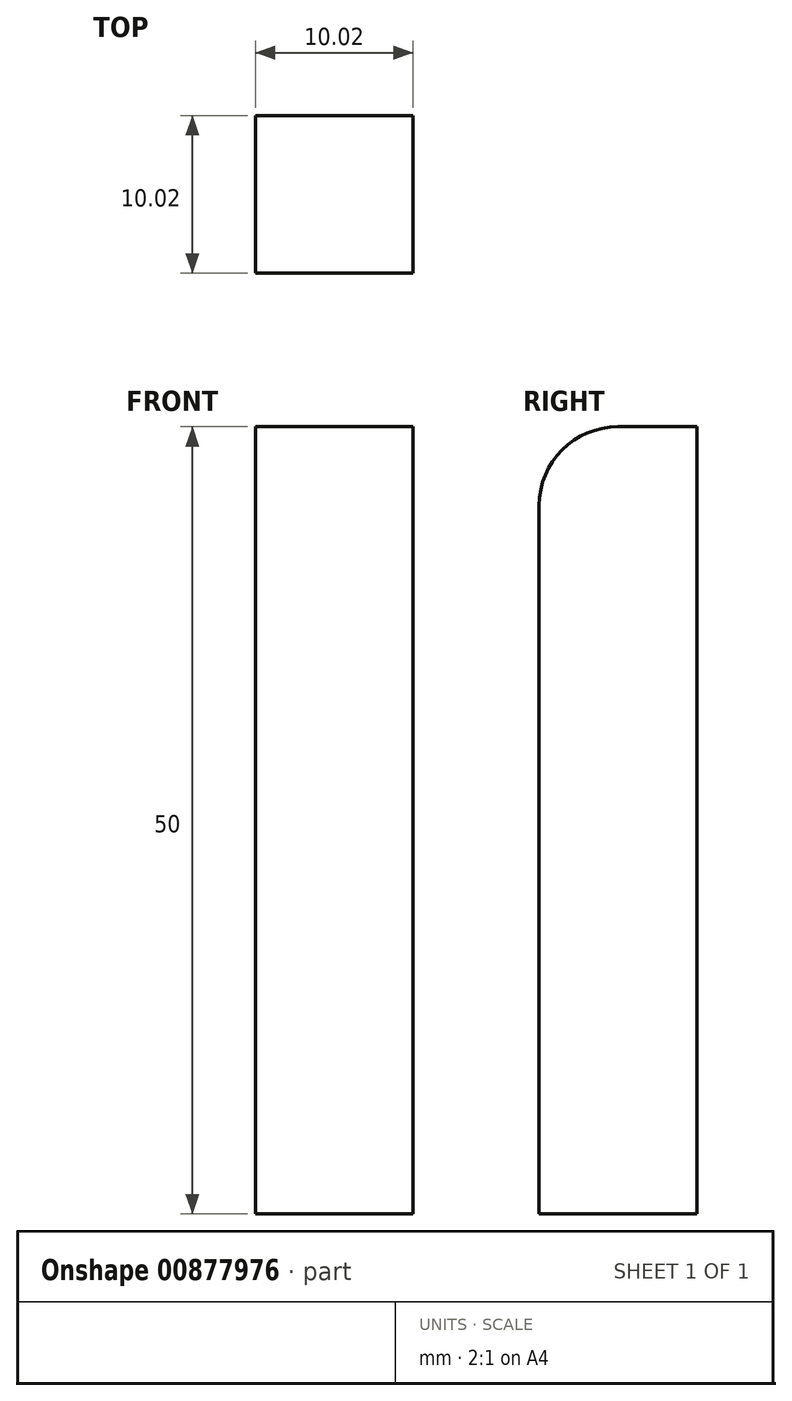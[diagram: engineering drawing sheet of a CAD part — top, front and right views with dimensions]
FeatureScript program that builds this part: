
annotation { "Feature Type Name" : "Feature", "Feature Type Description" : "" }
export const myFeature = defineFeature(function(context is Context, id is Id, definition is map)
    precondition{}
    {
        {
            var Q0;
            Q0=qCreatedBy(makeId("Top.planeOp"),FACE);
            var sketch = newSketch(context, id + "F0", { "sketchPlane" : qUnion([Q0])});
            skCircle(sketch, "E0", {"center": v(0, 0) * mm, "radius": 15 * mm});
            skSolve(sketch);
        }
        {
            var Q0;
            Q0=qSketchRegion(id+"F0",true);
            extrude(context, id + "F1", {"entities" : qUnion([Q0]), "endBound" : BoundingType.SYMMETRIC, "depth" : 25 * mm, "offsetDistance" : 25 * mm});
        }
        {
            var Q0;
            Q0=makeQuery(id+"F1.opExtrude","CAP_FACE",FACE,{"disambiguationData":[OSD([sQuery(id+"F0.wireOp",EDGE,"E0")])],"isStart":false});
            var sketch = newSketch(context, id + "F2", { "sketchPlane" : qUnion([Q0])});
            skLineSegment(sketch, "E1.bottom", {"start": v(5, -5) * mm, "end": v(-5, -5) * mm});
            skLineSegment(sketch, "E1.top", {"start": v(5, 5) * mm, "end": v(-5, 5) * mm});
            skLineSegment(sketch, "E1.left", {"start": v(5, -5) * mm, "end": v(5, 5) * mm});
            skLineSegment(sketch, "E1.right", {"start": v(-5, -5) * mm, "end": v(-5, 5) * mm});
            skPoint(sketch, "E1.middle", {"position": v(0, 0) * mm});
            skSolve(sketch);
        }
        {
            var Q0;
            Q0=qSketchRegion(id+"F2",true);
            extrude(context, id + "F3", {"entities" : qUnion([Q0]), "operationType" : NewBodyOperationType.ADD, "depth" : 25 * mm, "offsetDistance" : 25 * mm});
        }
        {
            var Q0;
            Q0=makeQuery(id+"F1.opExtrude","CAP_FACE",FACE,{"disambiguationData":[OSD([sQuery(id+"F0.wireOp",EDGE,"E0")])],"isStart":false});
            extrude(context, id + "F4", {"entities" : qUnion([Q0]), "operationType" : NewBodyOperationType.REMOVE, "oppositeDirection" : true, "depth" : 25 * mm, "offsetDistance" : 25 * mm});
        }
        {
            var Q0;
            Q0=makeQuery(id+"F3.opExtrude","CAP_EDGE",EDGE,{"disambiguationData":[OSD([sQuery(id+"F2.wireOp",EDGE,"E1.bottom")])],"isStart":false});
            fillet(context, id + "F5", {"entities" : qUnion([Q0]), "radius" : 5 * mm, "tangentPropagation" : true, "allowEdgeOverflow" : false});
        }
    });
